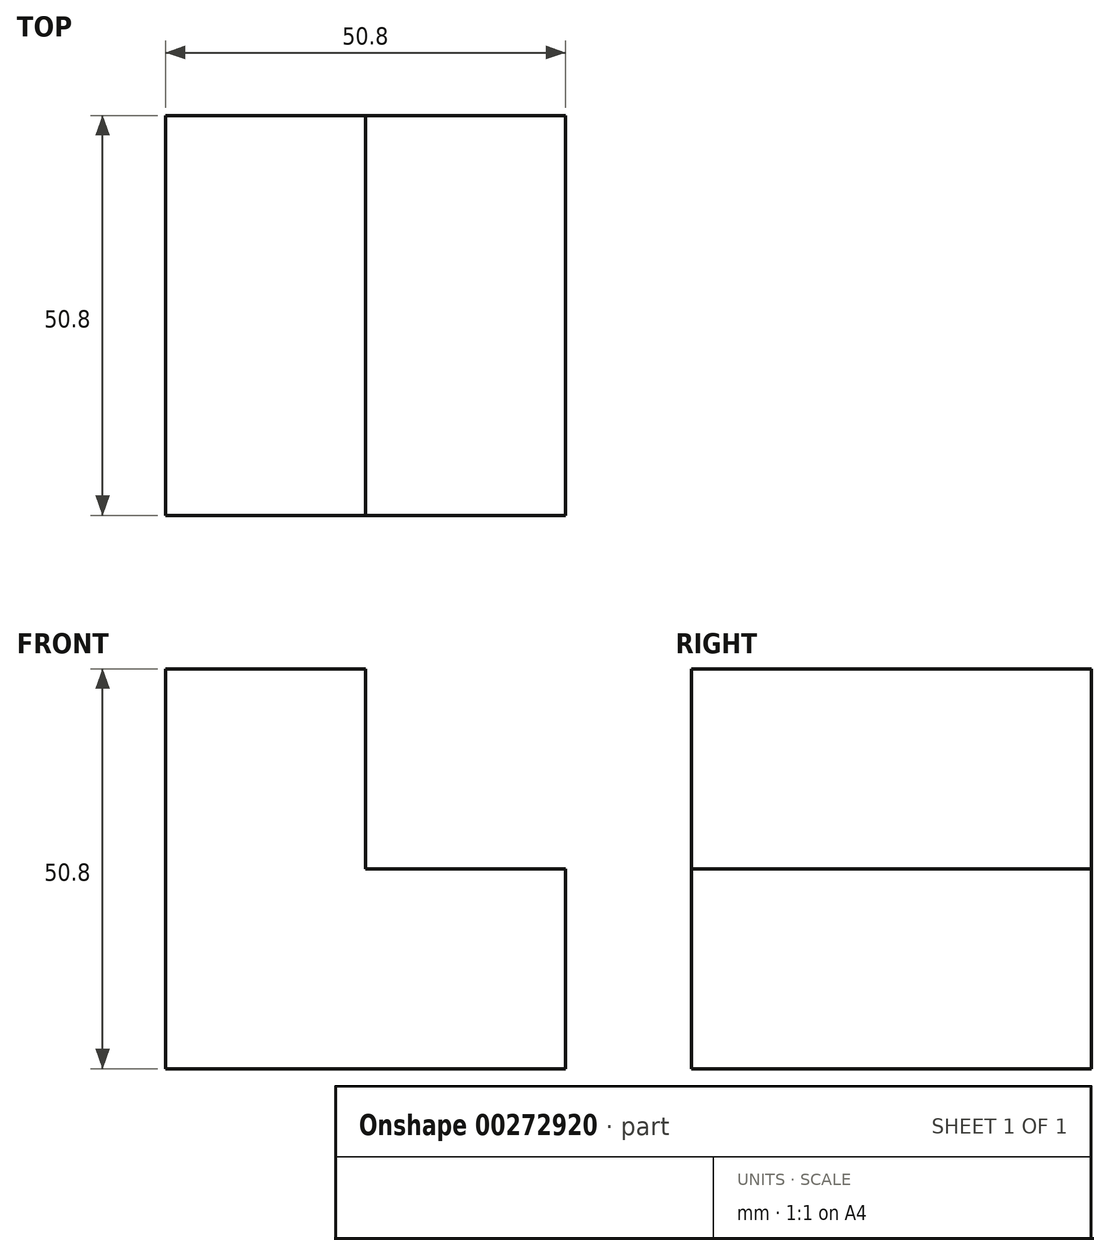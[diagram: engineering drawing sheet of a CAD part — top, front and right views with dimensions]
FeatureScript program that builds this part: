
annotation { "Feature Type Name" : "Feature", "Feature Type Description" : "" }
export const myFeature = defineFeature(function(context is Context, id is Id, definition is map)
    precondition{}
    {
        {
            var Q0;
            Q0=qCreatedBy(makeId("Front.planeOp"),FACE);
            var sketch = newSketch(context, id + "F0", { "sketchPlane" : qUnion([Q0])});
            skLineSegment(sketch, "E0", {"start": v(-50.8, 44.5) * mm, "end": v(-50.8, -6.3) * mm});
            skLineSegment(sketch, "E1", {"start": v(-50.8, -6.3) * mm, "end": v(0, -6.3) * mm});
            skLineSegment(sketch, "E2", {"start": v(-50.8, 44.5) * mm, "end": v(-25.4, 44.5) * mm});
            skLineSegment(sketch, "E3", {"start": v(-25.4, 44.5) * mm, "end": v(-25.4, 19.1) * mm});
            skLineSegment(sketch, "E4", {"start": v(-25.4, 19.1) * mm, "end": v(0, 19.1) * mm});
            skLineSegment(sketch, "E5", {"start": v(0, 19.1) * mm, "end": v(0, -6.3) * mm});
            skSolve(sketch);
        }
        {
            var Q0;
            Q0 = qSketchRegion(id + "F0", true);
            extrude(context, id + "F1", {"entities" : qUnion([Q0]), "depth" : 50.8 * mm});
        }
    });
